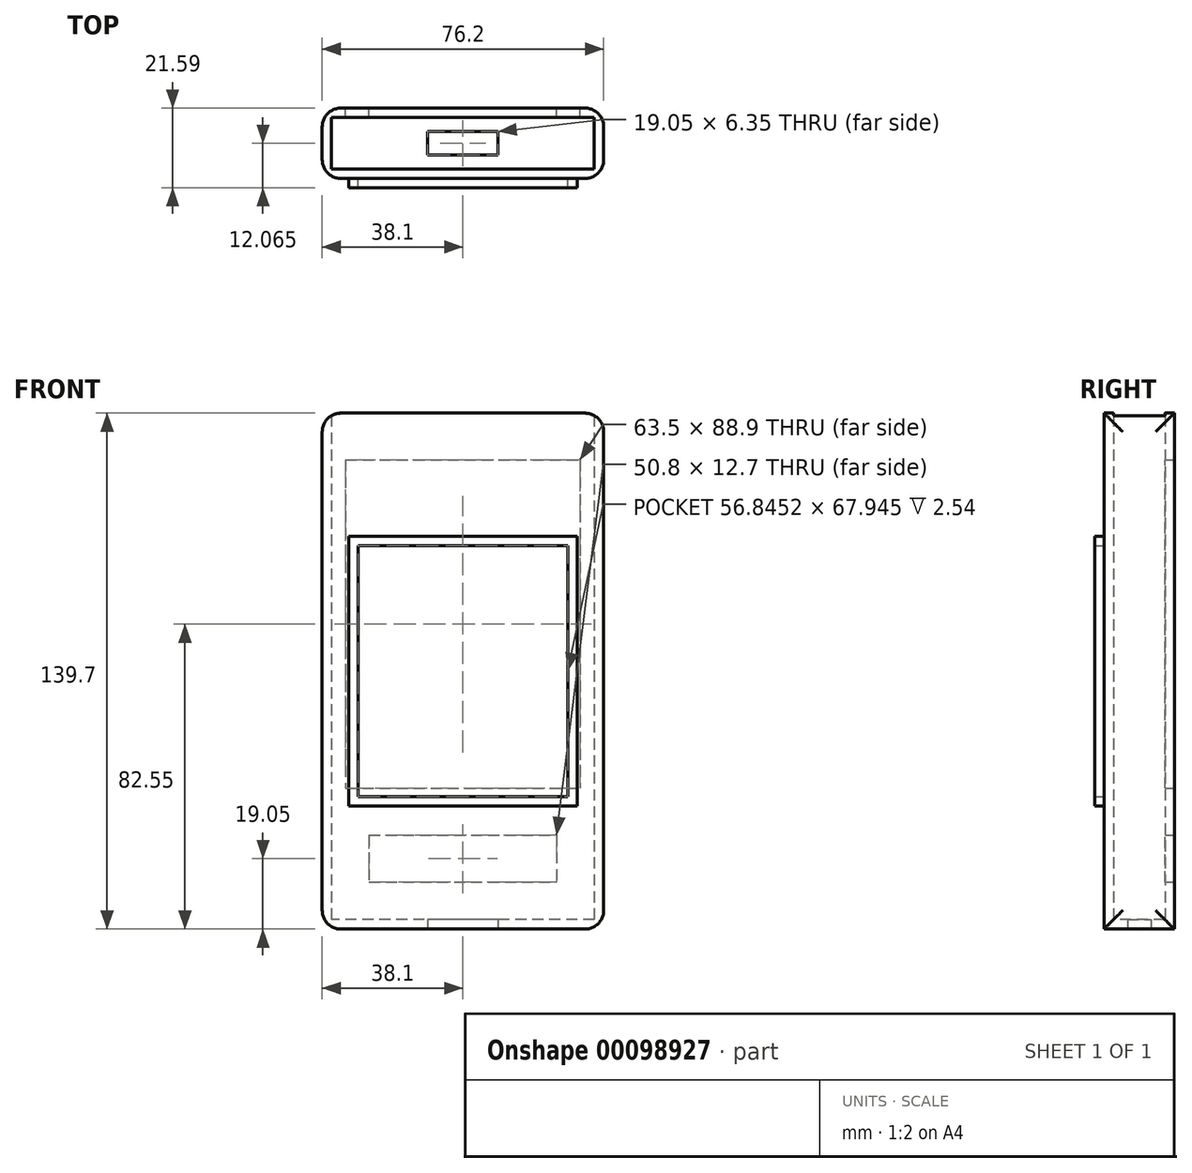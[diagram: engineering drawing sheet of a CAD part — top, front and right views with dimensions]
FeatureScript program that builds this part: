
annotation { "Feature Type Name" : "Feature", "Feature Type Description" : "" }
export const myFeature = defineFeature(function(context is Context, id is Id, definition is map)
    precondition{}
    {
        {
            var Q0;
            Q0=qCreatedBy(makeId("Front.planeOp"),FACE);
            var sketch = newSketch(context, id + "F0", { "sketchPlane" : qUnion([Q0])});
            skLineSegment(sketch, "E0.bottom", {"start": v(30.96, 36.51) * mm, "end": v(-30.96, 36.51) * mm});
            skLineSegment(sketch, "E0.top", {"start": v(30.96, -36.51) * mm, "end": v(-30.96, -36.51) * mm});
            skLineSegment(sketch, "E0.left", {"start": v(30.96, 36.51) * mm, "end": v(30.96, -36.51) * mm});
            skLineSegment(sketch, "E0.right", {"start": v(-30.96, 36.51) * mm, "end": v(-30.96, -36.51) * mm});
            skPoint(sketch, "E0.middle", {"position": v(0, 0) * mm});
            skSolve(sketch);
        }
        {
            var Q0;
            Q0=qSketchRegion(id+"F0",true);
            extrude(context, id + "F1", {"entities" : qUnion([Q0]), "depth" : 2.54 * mm});
        }
        {
            var Q0;
            Q0=makeQuery(id+"F1.opExtrude","CAP_FACE",FACE,{"disambiguationData":[OSD([sQuery(id+"F0.wireOp",EDGE,"E0.bottom"),sQuery(id+"F0.wireOp",EDGE,"E0.top"),sQuery(id+"F0.wireOp",EDGE,"E0.left"),sQuery(id+"F0.wireOp",EDGE,"E0.right")])],"isStart":false});
            shell(context, id + "F2", {"entities" : qUnion([Q0]), "thickness" : 2.54 * mm});
        }
        {
            var Q0;
            Q0=makeQuery(id+"F1.opExtrude","CAP_FACE",FACE,{"disambiguationData":[OSD([sQuery(id+"F0.wireOp",EDGE,"E0.bottom"),sQuery(id+"F0.wireOp",EDGE,"E0.top"),sQuery(id+"F0.wireOp",EDGE,"E0.left"),sQuery(id+"F0.wireOp",EDGE,"E0.right")])],"isStart":true});
            cPlane(context, id + "F3", {"entities" : qUnion([Q0]), "cplaneType" : CPlaneType.OFFSET, "offset" : 0 * mm, "width" : 152.4 * mm, "height" : 152.4 * mm});
        }
        {
            var Q0;
            Q0=qCreatedBy(id+"F3.planeOp",FACE);
            var sketch = newSketch(context, id + "F4", { "sketchPlane" : qUnion([Q0])});
            skLineSegment(sketch, "E1.bottom", {"start": v(-38.1, 69.85) * mm, "end": v(38.1, 69.85) * mm});
            skLineSegment(sketch, "E1.top", {"start": v(-38.1, -69.85) * mm, "end": v(38.1, -69.85) * mm});
            skLineSegment(sketch, "E1.left", {"start": v(-38.1, 69.85) * mm, "end": v(-38.1, -69.85) * mm});
            skLineSegment(sketch, "E1.right", {"start": v(38.1, 69.85) * mm, "end": v(38.1, -69.85) * mm});
            skPoint(sketch, "E1.middle", {"position": v(0, 0) * mm});
            skSolve(sketch);
        }
        {
            var Q0;
            Q0=qSketchRegion(id+"F4",true);
            extrude(context, id + "F5", {"entities" : qUnion([Q0]), "operationType" : NewBodyOperationType.ADD, "depth" : 19.05 * mm});
        }
        {
            var Q0;
            Q0=makeQuery(id+"F5.opExtrude","SWEPT_FACE",FACE,{"disambiguationData":[OSD([sQuery(id+"F4.wireOp",EDGE,"E1.bottom")])]});
            var Q1;
            Q1=makeQuery(id+"F1.opExtrude","SWEPT_BODY",BODY,{"disambiguationData":[OSD([sQuery(id+"F0.wireOp",EDGE,"E0.bottom"),sQuery(id+"F0.wireOp",EDGE,"E0.top"),sQuery(id+"F0.wireOp",EDGE,"E0.left"),sQuery(id+"F0.wireOp",EDGE,"E0.right")])]});
            shell(context, id + "F6", {"entities" : qUnion([Q0]), "parts" : qUnion([Q1]), "thickness" : 2.54 * mm});
        }
        {
            var Q0;
            Q0=makeQuery(id+"F5.opExtrude","SWEPT_FACE",FACE,{"disambiguationData":[OSD([sQuery(id+"F4.wireOp",EDGE,"E1.top")])]});
            var sketch = newSketch(context, id + "F7", { "sketchPlane" : qUnion([Q0])});
            skLineSegment(sketch, "E2.bottom", {"start": v(-9.52, -12.7) * mm, "end": v(9.52, -12.7) * mm});
            skLineSegment(sketch, "E2.top", {"start": v(-9.53, -6.35) * mm, "end": v(9.52, -6.35) * mm});
            skLineSegment(sketch, "E2.left", {"start": v(-9.53, -12.7) * mm, "end": v(-9.53, -6.35) * mm});
            skLineSegment(sketch, "E2.right", {"start": v(9.52, -12.7) * mm, "end": v(9.52, -6.35) * mm});
            skPoint(sketch, "E2.middle", {"position": v(0, -9.53) * mm});
            skPoint(sketch, "E2.middle.positionSnap0", {"position": v(38.1, -9.53) * mm});
            skPoint(sketch, "E2.centerSnap0", {"position": v(38.1, -9.53) * mm});
            skSolve(sketch);
        }
        {
            var Q0;
            Q0=qSketchRegion(id+"F7",true);
            extrude(context, id + "F8", {"entities" : qUnion([Q0]), "operationType" : NewBodyOperationType.REMOVE, "oppositeDirection" : true, "depth" : 25.4 * mm});
        }
        {
            var Q0;
            Q0=makeQuery(id+"F5.opExtrude","CAP_FACE",FACE,{"disambiguationData":[OSD([sQuery(id+"F4.wireOp",EDGE,"E1.bottom"),sQuery(id+"F4.wireOp",EDGE,"E1.top"),sQuery(id+"F4.wireOp",EDGE,"E1.left"),sQuery(id+"F4.wireOp",EDGE,"E1.right")])],"isStart":false});
            var sketch = newSketch(context, id + "F9", { "sketchPlane" : qUnion([Q0])});
            skLineSegment(sketch, "E3.bottom", {"start": v(31.75, 57.15) * mm, "end": v(-31.75, 57.15) * mm});
            skLineSegment(sketch, "E3.top", {"start": v(31.75, -31.75) * mm, "end": v(-31.75, -31.75) * mm});
            skLineSegment(sketch, "E3.left", {"start": v(31.75, 57.15) * mm, "end": v(31.75, -31.75) * mm});
            skLineSegment(sketch, "E3.right", {"start": v(-31.75, 57.15) * mm, "end": v(-31.75, -31.75) * mm});
            skPoint(sketch, "E3.middle", {"position": v(0, 12.7) * mm});
            skPoint(sketch, "E4.endSnap0", {"position": v(0, -31.75) * mm});
            skLineSegment(sketch, "E5.bottom", {"start": v(25.4, -44.45) * mm, "end": v(-25.4, -44.45) * mm});
            skLineSegment(sketch, "E5.top", {"start": v(25.4, -57.15) * mm, "end": v(-25.4, -57.15) * mm});
            skLineSegment(sketch, "E5.left", {"start": v(25.4, -44.45) * mm, "end": v(25.4, -57.15) * mm});
            skLineSegment(sketch, "E5.right", {"start": v(-25.4, -44.45) * mm, "end": v(-25.4, -57.15) * mm});
            skPoint(sketch, "E5.middle", {"position": v(0, -50.8) * mm});
            skSolve(sketch);
        }
        {
            var Q0;
            Q0=qSketchRegion(id+"F9",true);
            extrude(context, id + "F10", {"entities" : qUnion([Q0]), "operationType" : NewBodyOperationType.REMOVE, "endBound" : BoundingType.UP_TO_NEXT, "oppositeDirection" : true, "depth" : 25.4 * mm});
        }
        {
            var Q0;
            Q0=makeQuery(id+"F6.opShell","OFFSET_FACE",FACE,{"disambiguationData":[OSD([sQuery(id+"F0.wireOp",EDGE,"E0.bottom"),sQuery(id+"F0.wireOp",EDGE,"E0.top"),sQuery(id+"F0.wireOp",EDGE,"E0.left"),sQuery(id+"F0.wireOp",EDGE,"E0.right")])]});
            var sketch = newSketch(context, id + "F11", { "sketchPlane" : qUnion([Q0])});
            skLineSegment(sketch, "E6.bottom", {"start": v(28.42, 33.97) * mm, "end": v(-28.42, 33.97) * mm});
            skLineSegment(sketch, "E6.top", {"start": v(28.42, -33.97) * mm, "end": v(-28.42, -33.97) * mm});
            skLineSegment(sketch, "E6.left", {"start": v(28.42, 33.97) * mm, "end": v(28.42, -33.97) * mm});
            skLineSegment(sketch, "E6.right", {"start": v(-28.42, 33.97) * mm, "end": v(-28.42, -33.97) * mm});
            skPoint(sketch, "E6.middle", {"position": v(0, 0) * mm});
            skSolve(sketch);
        }
        {
            var Q0;
            Q0=qSketchRegion(id+"F11",true);
            var Q1;
            {var subQ0=sQuery(id+"F4.wireOp",EDGE,"E1.right");var subQ1=sQuery(id+"F4.wireOp",EDGE,"E1.left");var subQ2=sQuery(id+"F4.wireOp",EDGE,"E1.top");var subQ3=sQuery(id+"F4.wireOp",EDGE,"E1.bottom");Q1=makeQuery(id+"F6.opShell","OFFSET_FACE",FACE,{"disambiguationData":[OSD([subQ3,subQ2,subQ1,subQ0]),TDD([makeQuery(id+"F5.opExtrude","CAP_FACE",FACE,{"disambiguationData":[OSD([subQ3,subQ2,subQ1,subQ0])],"isStart":true})])]});}
            extrude(context, id + "F12", {"entities" : qUnion([Q0]), "operationType" : NewBodyOperationType.ADD, "endBound" : BoundingType.UP_TO_SURFACE, "endBoundEntityFace" : qUnion([Q1]), "depth" : 25.4 * mm});
        }
        {
            var Q0;
            Q0=makeQuery(id+"F1.opExtrude","CAP_FACE",FACE,{"disambiguationData":[OSD([sQuery(id+"F0.wireOp",EDGE,"E0.bottom"),sQuery(id+"F0.wireOp",EDGE,"E0.top"),sQuery(id+"F0.wireOp",EDGE,"E0.left"),sQuery(id+"F0.wireOp",EDGE,"E0.right")])],"isStart":false});
            shell(context, id + "F13", {"entities" : qUnion([Q0]), "thickness" : 2.54 * mm});
        }
        {
            var Q0;
            Q0=makeQuery(id+"F5.opExtrude","SWEPT_FACE",FACE,{"disambiguationData":[OSD([sQuery(id+"F4.wireOp",EDGE,"E1.right")])]});
            fillet(context, id + "F14", {"entities" : qUnion([Q0]), "radius" : 5.08 * mm, "tangentPropagation" : true, "allowEdgeOverflow" : false});
        }
        {
            var Q0;
            Q0=makeQuery(id+"F5.opExtrude","SWEPT_FACE",FACE,{"disambiguationData":[OSD([sQuery(id+"F4.wireOp",EDGE,"E1.left")])]});
            fillet(context, id + "F15", {"entities" : qUnion([Q0]), "radius" : 5.08 * mm, "tangentPropagation" : true, "allowEdgeOverflow" : false});
        }
    });
